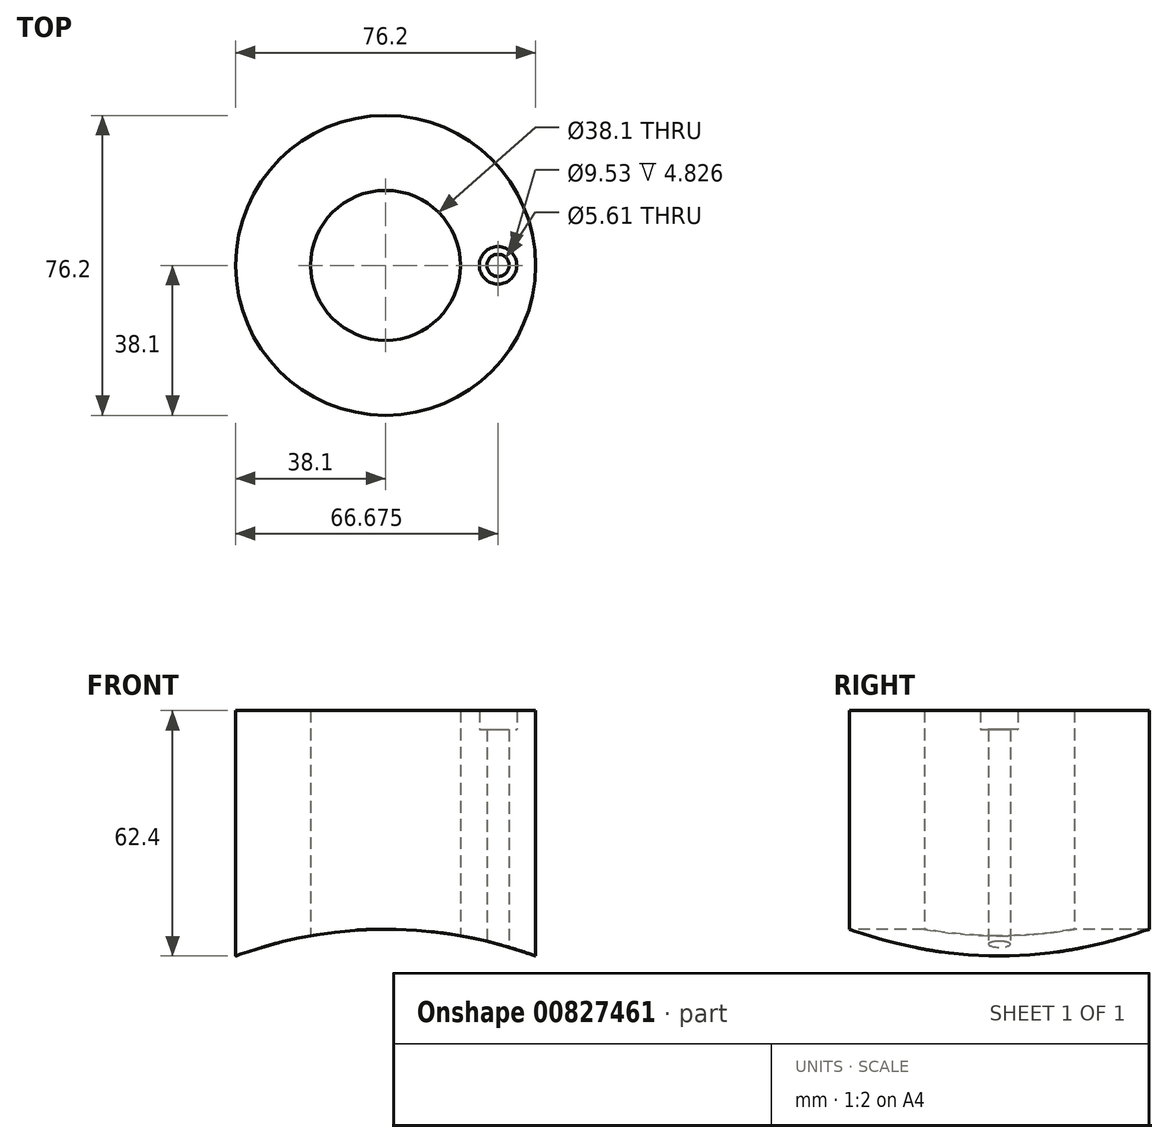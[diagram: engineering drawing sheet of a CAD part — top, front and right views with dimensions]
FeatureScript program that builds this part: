
annotation { "Feature Type Name" : "Feature", "Feature Type Description" : "" }
export const myFeature = defineFeature(function(context is Context, id is Id, definition is map)
    precondition{}
    {
        {
            var Q0;
            Q0=qCreatedBy(makeId("Top.planeOp"),FACE);
            var sketch = newSketch(context, id + "F0", { "sketchPlane" : qUnion([Q0])});
            skCircle(sketch, "E0", {"center": v(0, 0) * mm, "radius": 38.1 * mm});
            skCircle(sketch, "E1", {"center": v(0, 0) * mm, "radius": 19.05 * mm});
            skSolve(sketch);
        }
        {
            var Q0;
            Q0 = qSketchRegion(id + "F0", true);
            extrude(context, id + "F1", {"entities" : qUnion([Q0]), "depth" : 63.5 * mm, "offsetDistance" : 25.4 * mm});
        }
        {
            var Q0;
            Q0=qCreatedBy(makeId("Front.planeOp"),FACE);
            var sketch = newSketch(context, id + "F2", { "sketchPlane" : qUnion([Q0])});
            skLineSegment(sketch, "E2", {"start": v(28.58, 67.06) * mm, "end": v(28.58, -9.77) * mm, "construction": true});
            skLineSegment(sketch, "E3", {"start": v(28.58, 63.5) * mm, "end": v(23.81, 63.5) * mm});
            skLineSegment(sketch, "E4", {"start": v(23.81, 63.5) * mm, "end": v(23.81, 58.67) * mm});
            skLineSegment(sketch, "E5", {"start": v(23.81, 58.67) * mm, "end": v(25.77, 58.67) * mm});
            skLineSegment(sketch, "E6", {"start": v(25.77, 58.67) * mm, "end": v(25.77, 0) * mm});
            skLineSegment(sketch, "E7", {"start": v(25.77, 0) * mm, "end": v(28.58, 0) * mm});
            skLineSegment(sketch, "E8", {"start": v(28.58, 0) * mm, "end": v(28.58, 63.5) * mm});
            skLineSegment(sketch, "E9", {"start": v(0, 68.24) * mm, "end": v(0, 51.94) * mm, "construction": true});
            skSolve(sketch);
        }
        {
            var Q0;
            Q0 = qSketchRegion(id + "F2", true);
            var Q1;
            Q1=sQuery(id+"F2.wireOp",EDGE,"E2");
            revolve(context, id + "F3", {"operationType" : NewBodyOperationType.REMOVE, "surfaceOperationType" : NewSurfaceOperationType.NEW, "entities" : qUnion([Q0]), "axis" : qUnion([Q1]), "revolveType" : RevolveType.FULL, "oppositeDirection" : true});
        }
        {
            var Q0;
            Q0=qCreatedBy(makeId("Front.planeOp"),FACE);
            var sketch = newSketch(context, id + "F4", { "sketchPlane" : qUnion([Q0])});
            skCircle(sketch, "E10", {"center": v(0, -101.6) * mm, "radius": 109.54 * mm});
            skSolve(sketch);
        }
        {
            var Q0;
            Q0 = qSketchRegion(id + "F4", true);
            extrude(context, id + "F5", {"entities" : qUnion([Q0]), "operationType" : NewBodyOperationType.REMOVE, "endBound" : BoundingType.THROUGH_ALL, "oppositeDirection" : true, "depth" : 25.4 * mm, "offsetDistance" : 25.4 * mm, "hasSecondDirection" : true, "secondDirectionBound" : SecondDirectionBoundingType.THROUGH_ALL, "secondDirectionOppositeDirection" : false, "secondDirectionDepth" : 25.4 * mm});
        }
    });
